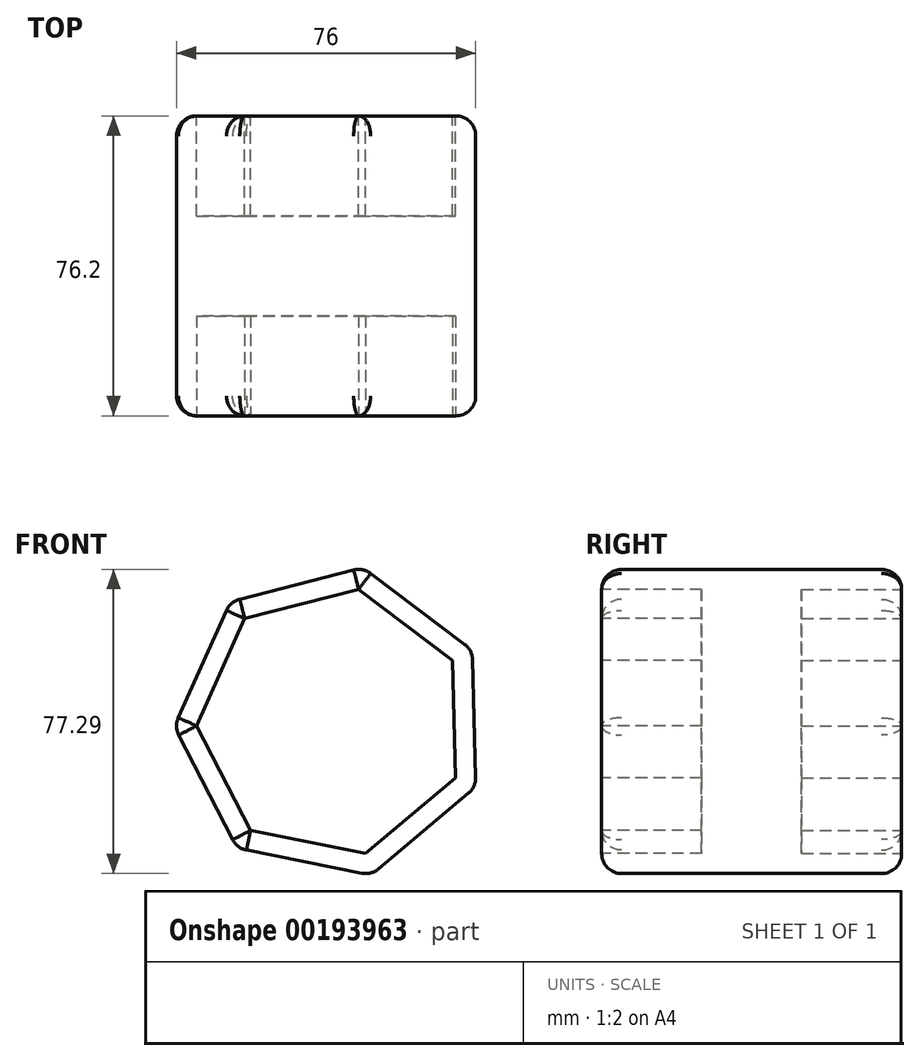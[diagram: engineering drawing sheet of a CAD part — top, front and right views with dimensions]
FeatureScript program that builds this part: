
annotation { "Feature Type Name" : "Feature", "Feature Type Description" : "" }
export const myFeature = defineFeature(function(context is Context, id is Id, definition is map)
    precondition{}
    {
        {
            var Q0;
            Q0=qCreatedBy(makeId("Front.planeOp"),FACE);
            var sketch = newSketch(context, id + "F0", { "sketchPlane" : qUnion([Q0])});
            skLineSegment(sketch, "E0.0", {"start": v(35.63, 17.38) * mm, "end": v(36.56, -17.38) * mm});
            skLineSegment(sketch, "E0.1", {"start": v(36.56, -17.38) * mm, "end": v(9.96, -39.79) * mm});
            skLineSegment(sketch, "E0.2", {"start": v(9.96, -39.79) * mm, "end": v(-24.14, -32.96) * mm});
            skLineSegment(sketch, "E0.3", {"start": v(-24.14, -32.96) * mm, "end": v(-40.06, -2.05) * mm});
            skLineSegment(sketch, "E0.4", {"start": v(-40.06, -2.05) * mm, "end": v(-25.82, 29.68) * mm});
            skLineSegment(sketch, "E0.5", {"start": v(-25.82, 29.68) * mm, "end": v(7.86, 38.33) * mm});
            skLineSegment(sketch, "E0.6", {"start": v(7.86, 38.33) * mm, "end": v(35.63, 17.38) * mm});
            skPoint(sketch, "E0.0.midPoint", {"position": v(36.1, 0) * mm});
            skSolve(sketch);
        }
        {
            var Q0;
            Q0=makeQuery(id+"F0.imprint","IMPRINT",FACE,{"disambiguationData":[TD([[makeQuery(id+"F0.imprint","IMPRINT",EDGE,{"derivedFrom":sQuery(id+"F0.wireOp",EDGE,"E0.0")}),-1.0]])]});
            extrude(context, id + "F1", {"entities" : qUnion([Q0]), "depth" : 76.2 * mm});
        }
        {
            var Q0;
            Q0=makeQuery(id+"F1.opExtrude","SWEPT_FACE",FACE,{"disambiguationData":[OSD([sQuery(id+"F0.wireOp",EDGE,"E0.5")])]});
            fillet(context, id + "F2", {"entities" : qUnion([Q0]), "radius" : 5.08 * mm, "tangentPropagation" : true, "allowEdgeOverflow" : false});
        }
        {
            var Q0;
            Q0=makeQuery(id+"F1.opExtrude","SWEPT_FACE",FACE,{"disambiguationData":[OSD([sQuery(id+"F0.wireOp",EDGE,"E0.6")])]});
            var Q1;
            Q1=makeQuery(id+"F1.opExtrude","SWEPT_FACE",FACE,{"disambiguationData":[OSD([sQuery(id+"F0.wireOp",EDGE,"E0.0")])]});
            var Q2;
            Q2=makeQuery(id+"F1.opExtrude","SWEPT_FACE",FACE,{"disambiguationData":[OSD([sQuery(id+"F0.wireOp",EDGE,"E0.1")])]});
            var Q3;
            Q3=makeQuery(id+"F1.opExtrude","SWEPT_FACE",FACE,{"disambiguationData":[OSD([sQuery(id+"F0.wireOp",EDGE,"E0.2")])]});
            var Q4;
            Q4=makeQuery(id+"F1.opExtrude","SWEPT_FACE",FACE,{"disambiguationData":[OSD([sQuery(id+"F0.wireOp",EDGE,"E0.4")])]});
            fillet(context, id + "F3", {"entities" : qUnion([Q0, Q1, Q2, Q3, Q4]), "radius" : 5.08 * mm, "tangentPropagation" : true, "allowEdgeOverflow" : false});
        }
        {
            var Q0;
            Q0=makeQuery(id+"F1.opExtrude","SWEPT_FACE",FACE,{"disambiguationData":[OSD([sQuery(id+"F0.wireOp",EDGE,"E0.3")])]});
            fillet(context, id + "F4", {"entities" : qUnion([Q0]), "radius" : 5.08 * mm, "tangentPropagation" : true, "allowEdgeOverflow" : false});
        }
        {
            var Q0;
            Q0=makeQuery(id+"F1.opExtrude","CAP_FACE",FACE,{"disambiguationData":[OSD([sQuery(id+"F0.wireOp",EDGE,"E0.0"),sQuery(id+"F0.wireOp",EDGE,"E0.1"),sQuery(id+"F0.wireOp",EDGE,"E0.2"),sQuery(id+"F0.wireOp",EDGE,"E0.3"),sQuery(id+"F0.wireOp",EDGE,"E0.4"),sQuery(id+"F0.wireOp",EDGE,"E0.5"),sQuery(id+"F0.wireOp",EDGE,"E0.6")])],"isStart":false});
            extrude(context, id + "F5", {"entities" : qUnion([Q0]), "operationType" : NewBodyOperationType.REMOVE, "oppositeDirection" : true, "depth" : 25.4 * mm});
        }
        {
            var Q0;
            Q0=makeQuery(id+"F1.opExtrude","CAP_FACE",FACE,{"disambiguationData":[OSD([sQuery(id+"F0.wireOp",EDGE,"E0.0"),sQuery(id+"F0.wireOp",EDGE,"E0.1"),sQuery(id+"F0.wireOp",EDGE,"E0.2"),sQuery(id+"F0.wireOp",EDGE,"E0.3"),sQuery(id+"F0.wireOp",EDGE,"E0.4"),sQuery(id+"F0.wireOp",EDGE,"E0.5"),sQuery(id+"F0.wireOp",EDGE,"E0.6")])],"isStart":true});
            extrude(context, id + "F6", {"entities" : qUnion([Q0]), "operationType" : NewBodyOperationType.REMOVE, "oppositeDirection" : true, "depth" : 25.4 * mm});
        }
    });
